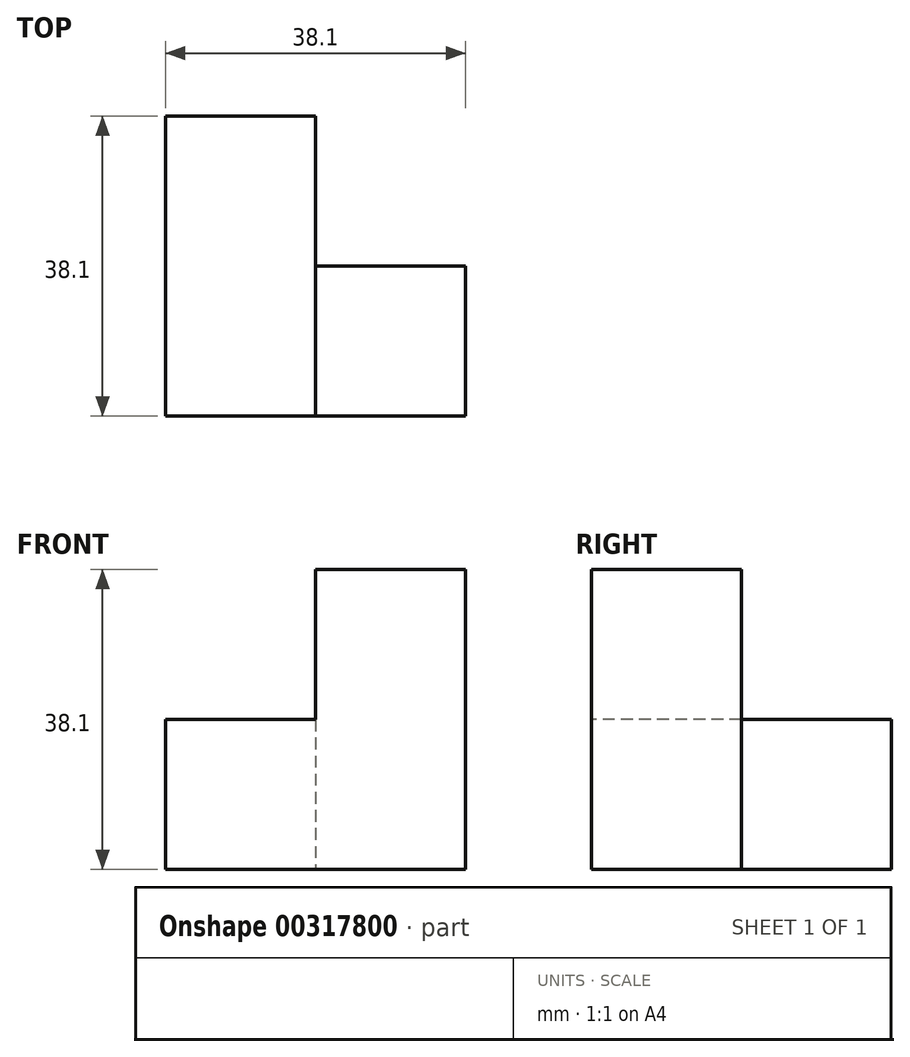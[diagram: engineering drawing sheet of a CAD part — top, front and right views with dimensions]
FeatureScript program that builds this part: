
annotation { "Feature Type Name" : "Feature", "Feature Type Description" : "" }
export const myFeature = defineFeature(function(context is Context, id is Id, definition is map)
    precondition{}
    {
        {
            var Q0;
            Q0=qCreatedBy(makeId("Top.planeOp"),FACE);
            var sketch = newSketch(context, id + "F0", { "sketchPlane" : qUnion([Q0])});
            skLineSegment(sketch, "E0.bottom", {"start": v(0, 0) * mm, "end": v(38.1, 0) * mm});
            skLineSegment(sketch, "E0.top", {"start": v(0, 38.1) * mm, "end": v(19.05, 38.1) * mm});
            skLineSegment(sketch, "E0.left", {"start": v(0, 0) * mm, "end": v(0, 38.1) * mm});
            skLineSegment(sketch, "E0.right", {"start": v(38.1, 0) * mm, "end": v(38.1, 19.05) * mm});
            skLineSegment(sketch, "E1", {"start": v(19.05, 38.1) * mm, "end": v(19.05, 19.05) * mm});
            skLineSegment(sketch, "E2", {"start": v(19.05, 19.05) * mm, "end": v(38.1, 19.05) * mm});
            skPoint(sketch, "E3.orphan", {"position": v(38.1, 38.1) * mm});
            skSolve(sketch);
        }
        {
            var Q0;
            Q0 = qSketchRegion(id + "F0", true);
            extrude(context, id + "F1", {"entities" : qUnion([Q0]), "depth" : 19.05 * mm});
        }
        {
            var Q0;
            Q0=makeQuery(id+"F1.opExtrude","CAP_FACE",FACE,{"disambiguationData":[OSD([sQuery(id+"F0.wireOp",EDGE,"E0.bottom"),sQuery(id+"F0.wireOp",EDGE,"E0.top"),sQuery(id+"F0.wireOp",EDGE,"E0.left"),sQuery(id+"F0.wireOp",EDGE,"E0.right"),sQuery(id+"F0.wireOp",EDGE,"E1"),sQuery(id+"F0.wireOp",EDGE,"E2")])],"isStart":false});
            var sketch = newSketch(context, id + "F2", { "sketchPlane" : qUnion([Q0])});
            skLineSegment(sketch, "E4.bottom", {"start": v(19.05, 19.05) * mm, "end": v(38.1, 19.05) * mm});
            skLineSegment(sketch, "E4.top", {"start": v(19.05, 0) * mm, "end": v(38.1, 0) * mm});
            skLineSegment(sketch, "E4.left", {"start": v(19.05, 19.05) * mm, "end": v(19.05, 0) * mm});
            skLineSegment(sketch, "E4.right", {"start": v(38.1, 19.05) * mm, "end": v(38.1, 0) * mm});
            skSolve(sketch);
        }
        {
            var Q0;
            Q0 = qSketchRegion(id + "F2", true);
            extrude(context, id + "F3", {"entities" : qUnion([Q0]), "operationType" : NewBodyOperationType.ADD, "depth" : 19.05 * mm});
        }
    });
